FCSTD DOCUMENT  (FreeCAD 0.21R33771 (Git))
Label: Rotor_MagnetJig_Assembly
License: All rights reserved
LicenseURL: http://en.wikipedia.org/wiki/All_rights_reserved
objects: App::Link×7, Part::FeaturePython×3, Spreadsheet::Sheet×1, App::Part×1
EXTERNAL_REF file=../../../Master_of_Puppets.FCStd obj=Alternator
EXTERNAL_REF file=../../../Master_of_Puppets.FCStd obj=Fastener
EXTERNAL_REF file=../../../Master_of_Puppets.FCStd obj=Hub
EXTERNAL_REF file=../../../Master_of_Puppets.FCStd obj=Spreadsheet
EXTERNAL_REF file=../Rotor_Disk_Back.FCStd obj=Pocket001Body
EXTERNAL_REF file=../Rotor_Disk_Back_ReducedWeight.FCStd obj=Body
EXTERNAL_REF file=Rotor_MagnetJig_Inner.FCStd obj=PolarPatternBody
EXTERNAL_REF file=Rotor_MagnetJig_Outer.FCStd obj=PolarPatternBody
EXTERNAL_REF file=../Rotor_Magnets.FCStd obj=Array
EXTERNAL_REF file=../../../Fasteners/Fastener_Bolt_HubHoles.FCStd obj=Binder
EXTERNAL_REF file=../../../Fasteners/Fastener_HexNut_HubHoles.FCStd obj=Binder
EXTERNAL_REF file=../../../Fasteners/Fastener_Washer_Hub.FCStd obj=Tube
EXTERNAL_REF file=Rotor_MagnetJig_Disk.FCStd obj=PocketBody

FEATURE [Spreadsheet::Sheet] Spreadsheet
  cells = A1='Inputs; A2='RotorDiskRadius; B2(RotorDiskRadius)==Master_of_Puppets#Spreadsheet.RotorDiskRadius; A3='MagnetThickness; B3(MagnetThickness)==Master_of_Puppets#Spreadsheet.MagnetThickness; A4='RotorDiskThickness; B4(RotorDiskThickness)==Master_of_Puppets#Spreadsheet.RotorDiskThickness; A5='VaneThickness; B5(VaneThickness)==Master_of_Puppets#Spreadsheet.VaneThickness; A6='InnerDistanceBetweenMagnets; B6(InnerDistanceBetweenMagnets)==Master_of_Puppets#Spreadsheet.InnerDistanceBetweenMagnets; A7='HubPitchCircleRadius; B7(HubPitchCircleRadius)==Master_of_Puppets#Hub.HubPitchCircleRadius; A8='RotorMoldBaseThickness; B8(RotorMoldBaseThickness)==Master_of_Puppets#Alternator.RotorMoldBaseThickness; A9='MagnetJigThickness; B9(MagnetJigThickness)==Master_of_Puppets#Alternator.MagnetJigThickness; A10='NumberOfRotorMoldBolts; B10(NumberOfRotorMoldBolts)==Master_of_Puppets#Alternator.NumberOfRotorMoldBolts; A11='WasherThickness; B11(WasherThickness)==Master_of_Puppets#Fastener.WasherThickness; A12='CoilType; B12(CoilType)==Master_of_Puppets#Spreadsheet.CoilType; A13='WeightReductionRotorDiskRadiusThreshold; B13(WeightReductionRotorDiskRadiusThreshold)==Master_of_Puppets#Alternator.WeightReductionRotorDiskRadiusThreshold; A14='Calculated; A15='InnerDistanceBetweenMagnetsThreshold; B15(InnerDistanceBetweenMagnetsThreshold)=10; A16='DistanceBetweenLayers; B16(DistanceBetweenLayers)=0; A17='BoltsZ; B17(BoltsZ)==DistanceBetweenLayers * -1; A18='MagnetsZ; B18(MagnetsZ)==RotorDiskThickness + DistanceBetweenLayers * 1; A19='ShowWashers; B19(ShowWashers)==InnerDistanceBetweenMagnets < InnerDistanceBetweenMagnetsThreshold ? 0 : 1; A20='WasherZ; B20(WasherZ)==RotorDiskThickness + DistanceBetweenLayers + DistanceBetweenLayers * ShowWashers; A21='WasherZOffset; B21(WasherZOffset)==ShowWashers == 1 ? WasherThickness : 0; A22='JigZ; B22(JigZ)==RotorDiskThickness + WasherZOffset + DistanceBetweenLayers * 2 + DistanceBetweenLayers * ShowWashers; A23='NutZ; B23(NutZ)==RotorDiskThickness + WasherZOffset + MagnetJigThickness + DistanceBetweenLayers * 4; A24='Rotor_MagnetJig; B24(Rotor_MagnetJig)==InnerDistanceBetweenMagnets < InnerDistanceBetweenMagnetsThreshold ? <<Rotor_MagnetJig_Outer>>#<<Rotor_MagnetJig>>._self : <<Rotor_MagnetJig_Inner>>#<<Rotor_MagnetJig>>._self; A25='Rotor_Disk_Back; B25(Rotor_Disk_Back)==RotorDiskRadius > WeightReductionRotorDiskRadiusThreshold ? <<Rotor_Disk_Back_ReducedWeight>>#<<Rotor_Disk_Back>>._self : <<Rotor_Disk_Back>>#<<Rotor_Disk_Back>>._self; A26='ShowMagnetJigDisk; B26(ShowMagnetJigDisk)==InnerDistanceBetweenMagnets < InnerDistanceBetweenMagnetsThreshold ? 1 : 0
FEATURE [App::Link] Link004  label="Rotor_MagnetJig"
  LinkPlacement = pos=(0,0,12.5) rot=(0,0,1;0rad)
  LinkedObject = -> <external Rotor_MagnetJig_Inner.FCStd>#PolarPatternBody
  Placement = pos=(0,0,12.5) rot=(0,0,1;0rad)
  expr: .Placement.Base.z = Spreadsheet.JigZ
  expr: LinkedObject = Spreadsheet.Rotor_MagnetJig
FEATURE [App::Link] Link  label="Rotor_Disk_Back"
  LinkedObject = -> <external ../Rotor_Disk_Back_ReducedWeight.FCStd>#Body
  expr: LinkedObject = Spreadsheet.Rotor_Disk_Back
FEATURE [App::Link] Link005  label="Rotor_Magnets"
  LinkPlacement = pos=(0,0,10) rot=(0,0,1;0rad)
  LinkedObject = -> <external ../Rotor_Magnets.FCStd>#Array
  Placement = pos=(0,0,10) rot=(0,0,1;0rad)
  expr: .Placement.Base.z = Spreadsheet.MagnetsZ
FEATURE [App::Link] Link006  label="Fastener_Bolt_HubHoles"
  LinkPlacement = pos=(0,65,0) rot=(0,0,1;0rad)
  LinkedObject = -> <external ../../../Fasteners/Fastener_Bolt_HubHoles.FCStd>#Binder
  Placement = pos=(0,65,0) rot=(0,0,1;0rad)
  Scale = -1
  ScaleVector = (-1,-1,-1)
  expr: .Placement.Base.y = Spreadsheet.HubPitchCircleRadius
FEATURE [App::Link] Link007  label="Fastener_HexNut_HubHoles"
  LinkPlacement = pos=(0,65,18.5) rot=(0,0,1;0rad)
  LinkedObject = -> <external ../../../Fasteners/Fastener_HexNut_HubHoles.FCStd>#Binder
  Placement = pos=(0,65,18.5) rot=(0,0,1;0rad)
  expr: .Placement.Base.y = Spreadsheet.HubPitchCircleRadius
  expr: .Placement.Base.z = Spreadsheet.NutZ
FEATURE [Part::FeaturePython] Array  label="Bolts"  # Draft array (typed FeaturePython)
  AlwaysSyncPlacement = false
  Angle = 360
  ArrayType = 1
  Axis = (0,0,1)
  Base = -> Link006
  Center = (0,0,0)
  Count = 5
  ExpandArray = false
  Fuse = false
  IntervalAxis = (0,0,0)
  IntervalX = (50,0,0)
  IntervalY = (0,50,0)
  IntervalZ = (0,0,50)
  NumberCircles = 3
  NumberPolar = 5
  NumberX = 2
  NumberY = 2
  NumberZ = 1
  PlacementList = 5 placements: [(0,65,0),(-61.8187,20.0861,0),(-38.206,-52.5861,0),(38.206,-52.5861,0),(61.8187,20.0861,0)]
  RadialDistance = 50
  ScaleList = (5) [(1,1,1),(1,1,1),(1,1,1),(1,1,1),(1,1,1)]
  Symmetry = 1
  TangentialDistance = 25
  expr: .Placement.Base.z = Spreadsheet.BoltsZ
  expr: NumberPolar = Spreadsheet.NumberOfRotorMoldBolts
FEATURE [Part::FeaturePython] Array001  label="Nuts"  # Draft array (typed FeaturePython)
  AlwaysSyncPlacement = false
  Angle = 360
  ArrayType = 1
  Axis = (0,0,1)
  Base = -> Link007
  Center = (0,0,0)
  Count = 5
  ExpandArray = false
  Fuse = false
  IntervalAxis = (0,0,0)
  IntervalX = (50,0,0)
  IntervalY = (0,50,0)
  IntervalZ = (0,0,50)
  NumberCircles = 3
  NumberPolar = 5
  NumberX = 2
  NumberY = 2
  NumberZ = 1
  PlacementList = 5 placements: [(0,65,18.5),(-61.8187,20.0861,18.5),(-38.206,-52.5861,18.5),(38.206,-52.5861,18.5),(61.8187,20.0861,18.5)]
  RadialDistance = 50
  ScaleList = (5) [(1,1,1),(1,1,1),(1,1,1),(1,1,1),(1,1,1)]
  Symmetry = 1
  TangentialDistance = 25
  expr: NumberPolar = Spreadsheet.NumberOfRotorMoldBolts
FEATURE [App::Link] Link008  label="Fastener_Washer_Hub"
  LinkPlacement = pos=(0,65,10) rot=(0,0,1;0rad)
  LinkedObject = -> <external ../../../Fasteners/Fastener_Washer_Hub.FCStd>#Tube
  Placement = pos=(0,65,10) rot=(0,0,1;0rad)
  expr: .Placement.Base.y = Spreadsheet.HubPitchCircleRadius
  expr: .Placement.Base.z = Spreadsheet.WasherZ
FEATURE [Part::FeaturePython] Array002  label="Washers"  # Draft array (typed FeaturePython)
  AlwaysSyncPlacement = false
  Angle = 360
  ArrayType = 1
  Axis = (0,0,1)
  Base = -> Link008
  Center = (0,0,0)
  Count = 5
  ExpandArray = false
  Fuse = false
  IntervalAxis = (0,0,0)
  IntervalX = (50,0,0)
  IntervalY = (0,50,0)
  IntervalZ = (0,0,50)
  NumberCircles = 3
  NumberPolar = 5
  NumberX = 2
  NumberY = 2
  NumberZ = 1
  PlacementList = 5 placements: [(0,65,10),(-61.8187,20.0861,10),(-38.206,-52.5861,10),(38.206,-52.5861,10),(61.8187,20.0861,10)]
  RadialDistance = 50
  ScaleList = (5) [(1,1,1),(1,1,1),(1,1,1),(1,1,1),(1,1,1)]
  Symmetry = 1
  TangentialDistance = 25
  expr: NumberPolar = Spreadsheet.NumberOfRotorMoldBolts
  expr: Visibility = Spreadsheet.ShowWashers
FEATURE [App::Link] Link009  label="Rotor_MagnetJig_Disk"
  LinkPlacement = pos=(0,0,12.5) rot=(0,0,1;0rad)
  LinkedObject = -> <external Rotor_MagnetJig_Disk.FCStd>#PocketBody
  Placement = pos=(0,0,12.5) rot=(0,0,1;0rad)
  expr: .Placement.Base.z = Spreadsheet.JigZ
  expr: Visibility = Spreadsheet.ShowMagnetJigDisk
FEATURE [App::Part] Part  label="Rotor_MagnetJig_Assembly"
  Group = -> [Link006,Array,Link,Link005,Link008,Array002,Link004,Link007,Array001,Link009]
  Origin = -> Origin

RESOLVED EXTERNAL PARTS (link-assembly join: the EXTERNAL_REF files above that resolve inside this repo's crawl, each included once):
---- part ../../../Fasteners/Fastener_Bolt_HubHoles.FCStd = doc fcstd_15687eb65cfb ----
FCSTD DOCUMENT  (FreeCAD 0.20R29177 (Git))
Label: Fastener_Bolt_HubHoles
License: All rights reserved
LicenseURL: http://en.wikipedia.org/wiki/All_rights_reserved
objects: PartDesign::SubShapeBinder×1
note: 1 computed .brp shape members not serialized (recipe doc carries the construction recipe); baked Part::Feature solids carry a one-line shape summary decoded from their .brp
EXTERNAL_REF file=Fastener_Bolt_Tail_Vane.FCStd obj=Body

FEATURE [PartDesign::SubShapeBinder] Binder  label="Fastener_Bolt_HubHoles"
  BindCopyOnChange = 2
  BindMode = 0
  ClaimChildren = false
  Fuse = false
  MakeFace = true
  OffsetFill = false
  OffsetIntersection = false
  OffsetJoinType = 0
  OffsetOpenResult = false
  PartialLoad = false
  Relative = true
  Support = -> [<external Fastener_Bolt_Tail_Vane.FCStd>#Body]
  Variant = 1
  _Version = 2
---- part ../../../Fasteners/Fastener_HexNut_HubHoles.FCStd = doc fcstd_dba15245a95b ----
FCSTD DOCUMENT  (FreeCAD 0.21R33771 (Git))
Label: Fastener_HexNut_HubHoles
License: All rights reserved
LicenseURL: http://en.wikipedia.org/wiki/All_rights_reserved
objects: PartDesign::SubShapeBinder×1
note: 1 computed .brp shape members not serialized (recipe doc carries the construction recipe); baked Part::Feature solids carry a one-line shape summary decoded from their .brp
EXTERNAL_REF file=Fastener_HexNut.FCStd obj=Body

FEATURE [PartDesign::SubShapeBinder] Binder  label="Fastener_HexNut"
  BindCopyOnChange = 2
  BindMode = 0
  ClaimChildren = false
  Fuse = false
  MakeFace = true
  OffsetFill = false
  OffsetIntersection = false
  OffsetJoinType = 0
  OffsetOpenResult = false
  PartialLoad = false
  Relative = true
  Support = -> [<external Fastener_HexNut.FCStd>#Body]
  Variant = 1
  _Version = 2
---- part ../../../Master_of_Puppets.FCStd = doc fcstd_6404554055c4 (61625 chars; too large to inline — full recipe in that document) ----
---- part ../Rotor_Disk_Back.FCStd = doc fcstd_76cebaedbb85 ----
FCSTD DOCUMENT  (FreeCAD 0.20R29177 (Git))
Label: Rotor_Disk_Back
License: All rights reserved
LicenseURL: http://en.wikipedia.org/wiki/All_rights_reserved
objects: Sketcher::SketchObject×3, PartDesign::Pocket×2, PartDesign::Pad×1, PartDesign::PolarPattern×1, Spreadsheet::Sheet×1, PartDesign::Body×1
note: 11 computed .brp shape members not serialized (recipe doc carries the construction recipe); baked Part::Feature solids carry a one-line shape summary decoded from their .brp
EXTERNAL_REF file=../../Master_of_Puppets.FCStd obj=Hub
EXTERNAL_REF file=../../Master_of_Puppets.FCStd obj=Spreadsheet

FEATURE [Sketcher::SketchObject] Sketch  label="DiskSketch"
  FullyConstrained = true
  MapMode = 5
  Support = -> [XY_Plane001]
  expr: Constraints[1] = Spreadsheet.RotorDiskRadius
  sketch-geometry (1):
    g0: Circle CenterX=0 CenterY=0 CenterZ=0 NormalX=0 NormalY=0 NormalZ=1 AngleXU=0 Radius=150
  constraints (2):
    c: Coincident(g0,g-1)
    c: Radius(g0) = 150
FEATURE [PartDesign::Pad] Pad  label="Disk"
  AllowMultiFace = false
  Direction = (0,0,1)
  Length = 10
  Length2 = 100
  Profile = -> Sketch
  Type = 0
  expr: Length = Spreadsheet.RotorDiskThickness
FEATURE [Sketcher::SketchObject] Sketch001  label="HubHoleSketch"
  FullyConstrained = true
  MapMode = 5
  Placement = pos=(0,0,10) rot=(0,0,1;0rad)
  Support = -> [Pad]
  expr: Constraints[3] = Spreadsheet.HubPitchCircleRadius
  expr: Constraints[4] = Spreadsheet.HubHolesRadius
  sketch-geometry (2):
    g0: LineSegment StartX=0 StartY=50 StartZ=0 EndX=0 EndY=0 EndZ=0
    g1: Circle CenterX=0 CenterY=50 CenterZ=0 NormalX=0 NormalY=0 NormalZ=1 AngleXU=0 Radius=6
  constraints (5):
    c: Coincident(g0,g-1)
    c: Vertical(g0)
    c: Coincident(g1,g0)
    c: Distance(g0) = 50
    c: Radius(g1) = 6
FEATURE [PartDesign::Pocket] Pocket
  AllowMultiFace = false
  BaseFeature = -> Pad
  Direction = (0,0,-1)
  Length = 5
  Length2 = 100
  Profile = -> Sketch001
  Type = 1
FEATURE [PartDesign::PolarPattern] PolarPattern  label="HubHolePolarPattern"
  Angle = 360
  Axis = -> Sketch001 [N_Axis]
  BaseFeature = -> Pocket
  Occurrences = 4
  Originals = -> [Pocket]
  expr: Occurrences = Spreadsheet.NumberOfHoles
FEATURE [Sketcher::SketchObject] Sketch002  label="CentralHoleSketch"
  FullyConstrained = true
  MapMode = 5
  Placement = pos=(0,0,10) rot=(0,0,1;0rad)
  Support = -> [PolarPattern]
  expr: Constraints[1] = Spreadsheet.RotorDiskCentralHoleRadius
  sketch-geometry (1):
    g0: Circle CenterX=0 CenterY=0 CenterZ=0 NormalX=0 NormalY=0 NormalZ=1 AngleXU=0 Radius=32.5
  constraints (2):
    c: Coincident(g0,g-1)
    c: Radius(g0) = 32.5
FEATURE [PartDesign::Pocket] Pocket001  label="CentralHole"
  AllowMultiFace = false
  BaseFeature = -> PolarPattern
  Direction = (0,0,-1)
  Length = 5
  Length2 = 100
  Profile = -> Sketch002
  Type = 1
FEATURE [Spreadsheet::Sheet] Spreadsheet
  cells = A1=Inputs; A2=RotorDiskRadius; B2(RotorDiskRadius)==Master_of_Puppets#Spreadsheet.RotorDiskRadius; A3=RotorDiskCentralHoleDiameter; B3(RotorDiskCentralHoleDiameter)==Master_of_Puppets#Spreadsheet.RotorDiskCentralHoleDiameter; A4=HubPitchCircleRadius; B4(HubPitchCircleRadius)==Master_of_Puppets#Hub.HubPitchCircleRadius; A5=RotorDiskThickness; B5(RotorDiskThickness)==Master_of_Puppets#Spreadsheet.RotorDiskThickness; A6=HubHolesRadius; B6(HubHolesRadius)==Master_of_Puppets#Hub.HubHolesRadius; A7=NumberOfHoles; B7(NumberOfHoles)==Master_of_Puppets#Hub.NumberOfHoles; A8=Calculated; A9=RotorDiskCentralHoleRadius; B9(RotorDiskCentralHoleRadius)==RotorDiskCentralHoleDiameter / 2
FEATURE [PartDesign::Body] Pocket001Body  label="Rotor_Disk_Back"
  Group = -> [Sketch,Pad,Sketch001,Pocket,PolarPattern,Sketch002,Pocket001]
  Openafpm_Flat = true
  Origin = -> Origin001
  Placement = pos=(4e-15,0,0) rot=(0,0,1;0rad)
  Tip = -> Pocket001
---- part ../Rotor_Disk_Back_ReducedWeight.FCStd = doc fcstd_80efc63f53a1 ----
FCSTD DOCUMENT  (FreeCAD 0.21R33771 (Git))
Label: Rotor_Disk_Back_ReducedWeight
License: All rights reserved
LicenseURL: http://en.wikipedia.org/wiki/All_rights_reserved
objects: Sketcher::SketchObject×3, PartDesign::Pocket×2, PartDesign::PolarPattern×2, PartDesign::Pad×1, Spreadsheet::Sheet×1, PartDesign::Mirrored×1, PartDesign::MultiTransform×1, PartDesign::Body×1
note: 14 computed .brp shape members not serialized (recipe doc carries the construction recipe); baked Part::Feature solids carry a one-line shape summary decoded from their .brp
EXTERNAL_REF file=../../Master_of_Puppets.FCStd obj=Alternator
EXTERNAL_REF file=../../Master_of_Puppets.FCStd obj=Hub
EXTERNAL_REF file=../../Master_of_Puppets.FCStd obj=Spreadsheet

FEATURE [Sketcher::SketchObject] Sketch  label="DiskSketch"
  FullyConstrained = true
  MapMode = 5
  Support = -> [XY_Plane]
  expr: Constraints[1] = Spreadsheet.RotorDiskRadius
  expr: Constraints[2] = Spreadsheet.RotorDiskCentralHoleRadius
  sketch-geometry (2):
    g0: Circle CenterX=0 CenterY=0 CenterZ=0 NormalX=0 NormalY=0 NormalZ=1 AngleXU=0 Radius=250
    g1: Circle CenterX=0 CenterY=0 CenterZ=0 NormalX=0 NormalY=0 NormalZ=1 AngleXU=0 Radius=47.5
  constraints (4):
    c: Coincident(g0,g-1)
    c: Radius(g0) = 250
    c: Radius(g1) = 47.5
    c: Coincident(g1,g0)
FEATURE [PartDesign::Pad] Pad  label="Disk"
  AllowMultiFace = false
  Direction = (0,0,1)
  Length = 10
  Length2 = 100
  Profile = -> Sketch
  Type = 0
  expr: Length = Spreadsheet.RotorDiskThickness
FEATURE [Sketcher::SketchObject] Sketch001  label="PocketSketch"
  FullyConstrained = true
  MapMode = 5
  Placement = pos=(0,0,10) rot=(0,0,1;0rad)
  Support = -> [Pad]
  expr: Constraints[12] = Spreadsheet.WidthOuterPocket / 2
  expr: Constraints[13] = Spreadsheet.WidthInnerPocket / 2
  expr: Constraints[2] = Spreadsheet.PocketOuterRadius
  expr: Constraints[3] = Spreadsheet.PocketInnerRadius
  sketch-geometry (6):
    g0: Circle CenterX=0 CenterY=0 CenterZ=0 NormalX=0 NormalY=0 NormalZ=1 AngleXU=0 Radius=86
    g1: Circle CenterX=0 CenterY=0 CenterZ=0 NormalX=0 NormalY=0 NormalZ=1 AngleXU=0 Radius=167
    g2: LineSegment StartX=22.5147 StartY=83.0005 StartZ=0 EndX=43.7205 EndY=161.175 EndZ=0
    g3: LineSegment StartX=5.3e-15 StartY=86 StartZ=0 EndX=5.3e-15 EndY=167 EndZ=0
    g4: ArcOfCircle CenterX=0 CenterY=5.0665e-12 CenterZ=0 NormalX=0 NormalY=0 NormalZ=1 AngleXU=0 Radius=86 StartAngle=1.30591 EndAngle=1.5708
    g5: ArcOfCircle CenterX=0 CenterY=5.0665e-12 CenterZ=0 NormalX=0 NormalY=0 NormalZ=1 AngleXU=0 Radius=167 StartAngle=1.30591 EndAngle=1.5708
  constraints (17):
    c: Coincident(g0,g-1)
    c: Coincident(g1,g-1)
    c: Radius(g1) = 167
    c: Radius(g0) = 86
    c: PointOnObject(g3,g0)
    c: PointOnObject(g3,g1)
    c: Vertical(g3)
    c: Coincident(g4,g2)
    c: Coincident(g4,g3)
    c: PointOnObject(g5,g-2)
    c: Coincident(g5,g2)
    c: Coincident(g5,g3)
    c: DistanceX(g-1,g2) = 43.7205
    c: DistanceX(g-1,g2) = 22.5147
    c: PointOnObject(g2,g1)
    c: DistanceX(g-1,g3) = 0
    c: Coincident(g4,g5)
FEATURE [PartDesign::Pocket] Pocket  label="PocketPocket"
  AllowMultiFace = false
  BaseFeature = -> Pad
  Direction = (0,0,-1)
  Length = 5
  Length2 = 100
  Profile = -> Sketch001
  Type = 1
FEATURE [Spreadsheet::Sheet] Spreadsheet
  cells = A1='Inputs; A2='Spreadsheet; A3='HubHolesRadius; B3(HubHolesRadius)==Master_of_Puppets#Hub.HubHolesRadius; A4='RotorDiskRadius; B4(RotorDiskRadius)==Master_of_Puppets#Spreadsheet.RotorDiskRadius; A5='RotorDiskCentralHoleDiameter; B5(RotorDiskCentralHoleDiameter)==Master_of_Puppets#Spreadsheet.RotorDiskCentralHoleDiameter; A6='HubPitchCircleRadius; B6(HubPitchCircleRadius)==Master_of_Puppets#Hub.HubPitchCircleRadius; A7='RotorDiskThickness; B7(RotorDiskThickness)==Master_of_Puppets#Spreadsheet.RotorDiskThickness; A8='Alternator; A9='NumberOfPockets; B9(NumberOfPockets)==Master_of_Puppets#Alternator.NumberOfPockets; A10='PocketInnerRadius; B10(PocketInnerRadius)==Master_of_Puppets#Alternator.PocketInnerRadius; A11='PocketOuterRadius; B11(PocketOuterRadius)==Master_of_Puppets#Alternator.PocketOuterRadius; A12='WidthInnerPocket; B12(WidthInnerPocket)==Master_of_Puppets#Alternator.WidthInnerPocket; A13='WidthOuterPocket; B13(WidthOuterPocket)==Master_of_Puppets#Alternator.WidthOuterPocket; A14='Hub; A15='NumberOfHoles; B15(NumberOfHoles)==Master_of_Puppets#Hub.NumberOfHoles; A16='Calculated; A17='RotorDiskCentralHoleRadius; B17(RotorDiskCentralHoleRadius)==RotorDiskCentralHoleDiameter / 2
FEATURE [Sketcher::SketchObject] Sketch002  label="HoleSketch"
  FullyConstrained = true
  MapMode = 5
  Placement = pos=(0,0,10) rot=(0,0,1;0rad)
  Support = -> [Pad]
  expr: Constraints[1] = Spreadsheet.HubPitchCircleRadius
  expr: Constraints[4] = Spreadsheet.HubHolesRadius
  sketch-geometry (2):
    g0: Circle CenterX=0 CenterY=0 CenterZ=0 NormalX=0 NormalY=0 NormalZ=1 AngleXU=0 Radius=65
    g1: Circle CenterX=0 CenterY=65 CenterZ=0 NormalX=0 NormalY=0 NormalZ=1 AngleXU=0 Radius=7
  constraints (5):
    c: Coincident(g0,g-1)
    c: Radius(g0) = 65
    c: PointOnObject(g1,g0)
    c: PointOnObject(g1,g-2)
    c: Radius(g1) = 7
FEATURE [PartDesign::Mirrored] Mirrored
  MirrorPlane = -> Sketch001 [V_Axis]
FEATURE [PartDesign::PolarPattern] PolarPattern
  Angle = 360
  Axis = -> Sketch001 [N_Axis]
  Occurrences = 6
  expr: Occurrences = Spreadsheet.NumberOfPockets
FEATURE [PartDesign::MultiTransform] MultiTransform  label="PocketMultiTransform"
  BaseFeature = -> Pocket
  Originals = -> [Pocket]
  Transformations = -> [Mirrored,PolarPattern]
FEATURE [PartDesign::Pocket] Pocket001  label="HolePocket"
  BaseFeature = -> MultiTransform
  Direction = (0,0,-1)
  Length = 5
  Length2 = 5
  Profile = -> Sketch002
  ReferenceAxis = -> Sketch002 [N_Axis]
  Type = 1
FEATURE [PartDesign::PolarPattern] PolarPattern001  label="HolePolarPattern"
  Angle = 360
  Axis = -> Sketch002 [N_Axis]
  BaseFeature = -> Pocket001
  Occurrences = 5
  Originals = -> [Pocket001]
  expr: Occurrences = Spreadsheet.NumberOfHoles
FEATURE [PartDesign::Body] Body  label="Rotor_Disk_Back"
  Group = -> [Sketch,Pad,Sketch001,Pocket,MultiTransform,Sketch002,Mirrored,PolarPattern,Pocket001,PolarPattern001]
  Openafpm_Flat = true
  Origin = -> Origin
  Tip = -> PolarPattern001
---- part ../Rotor_Magnets.FCStd = doc fcstd_047787b4cc6b ----
FCSTD DOCUMENT  (FreeCAD 0.20R29177 (Git))
Label: Rotor_Magnets
License: All rights reserved
LicenseURL: http://en.wikipedia.org/wiki/All_rights_reserved
objects: App::Link×1, Spreadsheet::Sheet×1, Part::FeaturePython×1
EXTERNAL_REF file=Rotor_Magnet.FCStd obj=Box
EXTERNAL_REF file=../../Master_of_Puppets.FCStd obj=Alternator
EXTERNAL_REF file=../../Master_of_Puppets.FCStd obj=Spreadsheet

FEATURE [App::Link] Link  label="Magnet"
  LinkPlacement = pos=(-25,97.902,0) rot=(0,0,1;0rad)
  LinkedObject = -> <external Rotor_Magnet.FCStd>#Box
  Placement = pos=(-25,97.902,0) rot=(0,0,1;0rad)
  expr: .Placement.Base.x = Spreadsheet.MagnetX
  expr: .Placement.Base.y = Spreadsheet.MagnetY
FEATURE [Spreadsheet::Sheet] Spreadsheet
  cells = A1=Inputs; A2=MagnetWidth; B2(MagnetWidth)==Master_of_Puppets#Spreadsheet.MagnetWidth; A3=MagnetLength; B3(MagnetLength)==Master_of_Puppets#Spreadsheet.MagnetLength; A4=RotorDiskRadius; B4(RotorDiskRadius)==Master_of_Puppets#Spreadsheet.RotorDiskRadius; A5=NumberMagnet; B5(NumberMagnet)==Master_of_Puppets#Spreadsheet.NumberMagnet; A6=DistanceOfMagnetFromCenter; B6(DistanceOfMagnetFromCenter)==Master_of_Puppets#Alternator.DistanceOfMagnetFromCenter; A7=Magnet; A8=MagnetX; B8(MagnetX)==-MagnetWidth / 2; A9=MagnetY; B9(MagnetY)==DistanceOfMagnetFromCenter
FEATURE [Part::FeaturePython] Array  label="Rotor_Magnets"  # Draft array (typed FeaturePython)
  AlwaysSyncPlacement = false
  Angle = 360
  ArrayType = 1
  Axis = (0,0,1)
  Base = -> Link
  Center = (0,0,0)
  Count = 12
  ExpandArray = false
  Fuse = false
  IntervalAxis = (0,0,0)
  IntervalX = (50,0,0)
  IntervalY = (0,50,0)
  IntervalZ = (0,0,50)
  NumberCircles = 3
  NumberPolar = 12
  NumberX = 2
  NumberY = 2
  NumberZ = 1
  Placement = pos=(3.6e-15,0,0) rot=(0,0,1;0rad)
  PlacementList = 12 placements: [(-25,97.902,0),(-70.6016,72.2856,0),(-97.2856,27.3004,0),(-97.902,-25,0),(-72.2856,-70.6016,0),(-27.3004,-97.2856,0),(25,-97.902,0),(70.6016,-72.2856,0),(97.2856,-27.3004,0),(97.902,25,0),(72.2856,70.6016,0),(27.3004,97.2856,0)]
  RadialDistance = 50
  ScaleList = (12) [(1,1,1),(1,1,1),(1,1,1),(1,1,1),(1,1,1),(1,1,1),(1,1,1),(1,1,1),(1,1,1),(1,1,1),(1,1,1),(1,1,1)]
  Symmetry = 1
  TangentialDistance = 25
  expr: NumberPolar = Spreadsheet.NumberMagnet
---- part Rotor_MagnetJig_Disk.FCStd = doc fcstd_5108bd749691 ----
FCSTD DOCUMENT  (FreeCAD 0.20R29177 (Git))
Label: Rotor_MagnetJig_Disk
Comment: Similar to Rotor_Mold_Island with varying radius and thickness.
License: All rights reserved
LicenseURL: http://en.wikipedia.org/wiki/All_rights_reserved
objects: Sketcher::SketchObject×2, PartDesign::Pad×1, PartDesign::Pocket×1, Spreadsheet::Sheet×1, PartDesign::PolarPattern×1, PartDesign::Body×1
note: 8 computed .brp shape members not serialized (recipe doc carries the construction recipe); baked Part::Feature solids carry a one-line shape summary decoded from their .brp
EXTERNAL_REF file=../../../Master_of_Puppets.FCStd obj=Alternator
EXTERNAL_REF file=../../../Master_of_Puppets.FCStd obj=Hub
EXTERNAL_REF file=../../../Master_of_Puppets.FCStd obj=Spreadsheet

FEATURE [Sketcher::SketchObject] Sketch
  FullyConstrained = true
  MapMode = 5
  Support = -> [XY_Plane001]
  expr: Constraints[1] = Spreadsheet.DistanceOfMagnetFromCenter
  sketch-geometry (1):
    g0: Circle CenterX=0 CenterY=0 CenterZ=0 NormalX=0 NormalY=0 NormalZ=1 AngleXU=0 Radius=103.248
  constraints (2):
    c: Coincident(g0,g-1)
    c: Radius(g0) = 103.248
FEATURE [PartDesign::Pad] Pad
  AllowMultiFace = false
  Direction = (0,0,1)
  Length = 6
  Length2 = 100
  Profile = -> Sketch
  Type = 0
  expr: Length = Spreadsheet.MagnetJigThickness
FEATURE [Sketcher::SketchObject] Sketch001
  FullyConstrained = true
  MapMode = 5
  Placement = pos=(0,0,6) rot=(0,0,1;0rad)
  Support = -> [Pad]
  expr: Constraints[3] = Spreadsheet.HubPitchCircleRadius
  expr: Constraints[4] = Spreadsheet.HubHolesRadius
  sketch-geometry (2):
    g0: LineSegment StartX=0 StartY=50 StartZ=0 EndX=0 EndY=0 EndZ=0
    g1: Circle CenterX=0 CenterY=50 CenterZ=0 NormalX=0 NormalY=0 NormalZ=1 AngleXU=0 Radius=6
  constraints (5):
    c: Coincident(g0,g-1)
    c: Vertical(g0)
    c: Coincident(g1,g0)
    c: Distance(g0) = 50
    c: Radius(g1) = 6
FEATURE [PartDesign::Pocket] Pocket
  AllowMultiFace = false
  BaseFeature = -> Pad
  Direction = (0,0,-1)
  Length = 5
  Length2 = 100
  Profile = -> Sketch001
  Type = 1
FEATURE [Spreadsheet::Sheet] Spreadsheet
  cells = A1=Inputs; A2=HubHolesRadius; B2(HubHolesRadius)==Master_of_Puppets#Hub.HubHolesRadius; A3=HubPitchCircleRadius; B3(HubPitchCircleRadius)==Master_of_Puppets#Hub.HubPitchCircleRadius; A4=MagnetThickness; B4(MagnetThickness)==Master_of_Puppets#Spreadsheet.MagnetThickness; A5=NumberOfRotorMoldBolts; B5(NumberOfRotorMoldBolts)==Master_of_Puppets#Alternator.NumberOfRotorMoldBolts; A6=MagnetJigThickness; B6(MagnetJigThickness)==Master_of_Puppets#Alternator.MagnetJigThickness; A7=DistanceOfMagnetFromCenter; B7(DistanceOfMagnetFromCenter)==Master_of_Puppets#Alternator.DistanceOfMagnetFromCenter
FEATURE [PartDesign::PolarPattern] PolarPattern
  Angle = 360
  Axis = -> Sketch001 [N_Axis]
  BaseFeature = -> Pocket
  Occurrences = 2
  Originals = -> [Pocket]
  expr: Occurrences = Spreadsheet.NumberOfRotorMoldBolts
FEATURE [PartDesign::Body] PocketBody  label="Rotor_MagnetJig_Disk"
  Group = -> [Sketch,Pad,Sketch001,Pocket,PolarPattern]
  Openafpm_Flat = true
  Origin = -> Origin001
  Tip = -> PolarPattern
---- part Rotor_MagnetJig_Inner.FCStd = doc fcstd_12b98af02b98 ----
FCSTD DOCUMENT  (FreeCAD 0.20R29177 (Git))
Label: Rotor_MagnetJig_Inner
License: All rights reserved
LicenseURL: http://en.wikipedia.org/wiki/All_rights_reserved
objects: Sketcher::SketchObject×3, PartDesign::Pocket×2, PartDesign::PolarPattern×2, PartDesign::Pad×1, Spreadsheet::Sheet×1, PartDesign::Body×1
note: 12 computed .brp shape members not serialized (recipe doc carries the construction recipe); baked Part::Feature solids carry a one-line shape summary decoded from their .brp
EXTERNAL_REF file=../../../Master_of_Puppets.FCStd obj=Alternator
EXTERNAL_REF file=../../../Master_of_Puppets.FCStd obj=Hub
EXTERNAL_REF file=../../../Master_of_Puppets.FCStd obj=Spreadsheet

FEATURE [Sketcher::SketchObject] Sketch  label="RotorDiskSketch"
  FullyConstrained = true
  MapMode = 5
  Support = -> [XY_Plane001]
  expr: Constraints[1] = Spreadsheet.RotorDiskRadius
  sketch-geometry (1):
    g0: Circle CenterX=0 CenterY=0 CenterZ=0 NormalX=0 NormalY=0 NormalZ=1 AngleXU=0 Radius=150
  constraints (2):
    c: Coincident(g0,g-1)
    c: Radius(g0) = 150
FEATURE [PartDesign::Pad] Pad  label="RotorDiskPad"
  AllowMultiFace = false
  Direction = (0,0,1)
  Length = 6
  Length2 = 100
  Profile = -> Sketch
  Type = 0
  expr: Length = Spreadsheet.MagnetJigThickness
FEATURE [Sketcher::SketchObject] Sketch001  label="HolesSketch"
  FullyConstrained = true
  MapMode = 5
  Placement = pos=(0,0,6) rot=(0,0,1;0rad)
  Support = -> [Pad]
  expr: Constraints[1] = Spreadsheet.HubHolesRadius
  expr: Constraints[2] = Spreadsheet.HubPitchCircleRadius
  sketch-geometry (1):
    g0: Circle CenterX=0 CenterY=50 CenterZ=0 NormalX=0 NormalY=0 NormalZ=1 AngleXU=0 Radius=6
  constraints (3):
    c: PointOnObject(g0,g-2)
    c: Radius(g0) = 6
    c: DistanceY(g-1,g0) = 50
FEATURE [PartDesign::Pocket] Pocket  label="HolesPocket"
  AllowMultiFace = false
  BaseFeature = -> Pad
  Direction = (0,0,-1)
  Length = 5
  Length2 = 100
  Profile = -> Sketch001
  Type = 1
FEATURE [Sketcher::SketchObject] Sketch002  label="MagnetSketch"
  FullyConstrained = true
  MapMode = 5
  Placement = pos=(0,0,6) rot=(0,0,1;0rad)
  Support = -> [Pocket]
  expr: Constraints[4] = Spreadsheet.MagnetWidth
  expr: Constraints[5] = Spreadsheet.MagnetLength
  expr: Constraints[7] = Spreadsheet.RotorDiskRadius
  sketch-geometry (5):
    g0: LineSegment StartX=15 StartY=150 StartZ=0 EndX=15 EndY=104 EndZ=0
    g1: LineSegment StartX=15 StartY=104 StartZ=0 EndX=-15 EndY=104 EndZ=0
    g2: LineSegment StartX=-15 StartY=104 StartZ=0 EndX=-15 EndY=150 EndZ=0
    g3: Circle CenterX=0 CenterY=0 CenterZ=0 NormalX=0 NormalY=0 NormalZ=1 AngleXU=0 Radius=150
    g4: LineSegment StartX=-15 StartY=150 StartZ=0 EndX=15 EndY=150 EndZ=0
  constraints (13):
    c: Coincident(g0,g1)
    c: Coincident(g1,g2)
    c: Vertical(g0)
    c: Vertical(g2)
    c: DistanceX(g2,g0) = 30
    c: DistanceY(g2,g2) = 46
    c: Coincident(g3,g-1)
    c: Radius(g3) = 150
    c: Coincident(g4,g2)
    c: Coincident(g4,g0)
    c: Horizontal(g4)
    c: Tangent(g4,g3)
    c: Symmetric(g0,g1,g-2)
FEATURE [PartDesign::Pocket] Pocket001  label="MagnetPocket"
  AllowMultiFace = false
  BaseFeature = -> Pocket
  Direction = (0,0,-1)
  Length = 5
  Length2 = 100
  Profile = -> Sketch002
  Type = 1
FEATURE [PartDesign::PolarPattern] PolarPattern  label="MagnetPolarPattern"
  Angle = 360
  Axis = -> Sketch002 [N_Axis]
  BaseFeature = -> Pocket001
  Occurrences = 12
  Originals = -> [Pocket001]
  expr: Occurrences = Spreadsheet.NumberMagnet
FEATURE [Spreadsheet::Sheet] Spreadsheet
  cells = A1=Inputs; A2=RotorDiskRadius; B2(RotorDiskRadius)==Master_of_Puppets#Spreadsheet.RotorDiskRadius; A3=HubHolesRadius; B3(HubHolesRadius)==Master_of_Puppets#Hub.HubHolesRadius; A4=HubPitchCircleRadius; B4(HubPitchCircleRadius)==Master_of_Puppets#Hub.HubPitchCircleRadius; A5=MagnetWidth; B5(MagnetWidth)==Master_of_Puppets#Spreadsheet.MagnetWidth; A6=MagnetLength; B6(MagnetLength)==Master_of_Puppets#Spreadsheet.MagnetLength; A7=NumberMagnet; B7(NumberMagnet)==Master_of_Puppets#Spreadsheet.NumberMagnet; A8=NumberOfRotorMoldBolts; B8(NumberOfRotorMoldBolts)==Master_of_Puppets#Alternator.NumberOfRotorMoldBolts; A9=MagnetJigThickness; B9(MagnetJigThickness)==Master_of_Puppets#Alternator.MagnetJigThickness
FEATURE [PartDesign::PolarPattern] PolarPattern001  label="HolesPolarPattern"
  Angle = 360
  Axis = -> Sketch001 [N_Axis]
  BaseFeature = -> PolarPattern
  Occurrences = 2
  Originals = -> [Pocket]
  expr: Occurrences = Spreadsheet.NumberOfRotorMoldBolts
FEATURE [PartDesign::Body] PolarPatternBody  label="Rotor_MagnetJig"
  Group = -> [Sketch,Pad,Sketch001,Pocket,Sketch002,Pocket001,PolarPattern,PolarPattern001]
  Openafpm_Flat = true
  Origin = -> Origin001
  Tip = -> PolarPattern001
---- part Rotor_MagnetJig_Outer.FCStd = doc fcstd_f523b8629cb4 ----
FCSTD DOCUMENT  (FreeCAD 0.20R29177 (Git))
Label: Rotor_MagnetJig_Outer
License: All rights reserved
LicenseURL: http://en.wikipedia.org/wiki/All_rights_reserved
objects: Sketcher::SketchObject×3, PartDesign::Pocket×2, Spreadsheet::Sheet×1, PartDesign::Pad×1, PartDesign::PolarPattern×1, PartDesign::Body×1
note: 11 computed .brp shape members not serialized (recipe doc carries the construction recipe); baked Part::Feature solids carry a one-line shape summary decoded from their .brp
EXTERNAL_REF file=../../../Master_of_Puppets.FCStd obj=Alternator
EXTERNAL_REF file=../../../Master_of_Puppets.FCStd obj=Spreadsheet

FEATURE [Sketcher::SketchObject] Sketch002  label="MagnetSketch"
  FullyConstrained = true
  MapMode = 5
  Placement = pos=(0,0,6) rot=(0,0,1;0rad)
  expr: .Placement.Base.z = Spreadsheet.MagnetJigThickness
  expr: Constraints[13] = Spreadsheet.DistanceOfMagnetFromCenter
  expr: Constraints[4] = Spreadsheet.MagnetWidth
  expr: Constraints[5] = Spreadsheet.MagnetLength
  sketch-geometry (5):
    g0: LineSegment StartX=25 StartY=147.902 StartZ=0 EndX=25 EndY=97.902 EndZ=0
    g1: LineSegment StartX=25 StartY=97.902 StartZ=0 EndX=-25 EndY=97.902 EndZ=0
    g2: LineSegment StartX=-25 StartY=97.902 StartZ=0 EndX=-25 EndY=147.902 EndZ=0
    g3: LineSegment StartX=-25 StartY=147.902 StartZ=0 EndX=25 EndY=147.902 EndZ=0
    g4: LineSegment StartX=0 StartY=0 StartZ=0 EndX=0 EndY=97.902 EndZ=0
  constraints (14):
    c: Coincident(g0,g1)
    c: Coincident(g1,g2)
    c: Vertical(g0)
    c: Vertical(g2)
    c: DistanceX(g2,g0) = 50
    c: DistanceY(g2,g2) = 50
    c: Coincident(g3,g2)
    c: Coincident(g3,g0)
    c: Horizontal(g3)
    c: Symmetric(g0,g1,g-2)
    c: Coincident(g4,g-1)
    c: PointOnObject(g4,g1)
    c: Vertical(g4)
    c: DistanceY(g4,g4) = 97.902
FEATURE [Spreadsheet::Sheet] Spreadsheet
  cells = A1=Inputs; A2=RotorDiskRadius; B2(RotorDiskRadius)==Master_of_Puppets#Spreadsheet.RotorDiskRadius; A3=MagnetWidth; B3(MagnetWidth)==Master_of_Puppets#Spreadsheet.MagnetWidth; A4=MagnetLength; B4(MagnetLength)==Master_of_Puppets#Spreadsheet.MagnetLength; A5=NumberMagnet; B5(NumberMagnet)==Master_of_Puppets#Spreadsheet.NumberMagnet; A6=RotorMoldSideLength; B6(RotorMoldSideLength)==Master_of_Puppets#Alternator.RotorMoldSideLength; A7=MagnetJigThickness; B7(MagnetJigThickness)==Master_of_Puppets#Alternator.MagnetJigThickness; A8=DistanceOfMagnetFromCenter; B8(DistanceOfMagnetFromCenter)==Master_of_Puppets#Alternator.DistanceOfMagnetFromCenter; A9=Calculated; A10=Inradius; B10(Inradius)==DistanceOfMagnetFromCenter; A11=SideLength; B11(SideLength)==2 * Inradius * tan(180 / NumberMagnet); C11=https://keisan.casio.com/exec/system/1223432660; A12=InnerHoleRadius; B12(InnerHoleRadius)==SideLength / (2 * sin(180 / NumberMagnet)); C12=https://www-formula.com/geometry/radius-circumcircle/radius-circumcircle-regular-polygon
FEATURE [Sketcher::SketchObject] Sketch  label="SquareSketch"
  FullyConstrained = true
  MapMode = 5
  Support = -> [XY_Plane001]
  expr: Constraints[6] = Spreadsheet.RotorMoldSideLength
  sketch-geometry (4):
    g0: LineSegment StartX=-199.995 StartY=-199.995 StartZ=0 EndX=199.995 EndY=-199.995 EndZ=0
    g1: LineSegment StartX=199.995 StartY=-199.995 StartZ=0 EndX=199.995 EndY=199.995 EndZ=0
    g2: LineSegment StartX=199.995 StartY=199.995 StartZ=0 EndX=-199.995 EndY=199.995 EndZ=0
    g3: LineSegment StartX=-199.995 StartY=199.995 StartZ=0 EndX=-199.995 EndY=-199.995 EndZ=0
  constraints (10):
    c: Coincident(g0,g1)
    c: Coincident(g1,g2)
    c: Coincident(g2,g3)
    c: Coincident(g3,g0)
    c: Horizontal(g2)
    c: Vertical(g3)
    c: DistanceX(g2,g2) = 399.99
    c: Equal(g3,g0)
    c: Symmetric(g1,g0,g-1)
    c: Symmetric(g0,g0,g-2)
FEATURE [PartDesign::Pad] Pad  label="SquarePad"
  AllowMultiFace = false
  Direction = (0,0,1)
  Length = 6
  Length2 = 100
  Profile = -> Sketch
  Type = 0
  expr: Length = Spreadsheet.MagnetJigThickness
FEATURE [PartDesign::Pocket] Pocket001  label="MagnetPocket"
  AllowMultiFace = false
  BaseFeature = -> Pad
  Direction = (0,0,-1)
  Length = 5
  Length2 = 100
  Profile = -> Sketch002
  Type = 1
FEATURE [PartDesign::PolarPattern] PolarPattern  label="MagnetPolarPattern"
  Angle = 360
  Axis = -> Sketch002 [N_Axis]
  BaseFeature = -> Pocket001
  Occurrences = 12
  Originals = -> [Pocket001]
  expr: Occurrences = Spreadsheet.NumberMagnet
FEATURE [Sketcher::SketchObject] Sketch003  label="InnerHoleSketch"
  FullyConstrained = true
  MapMode = 5
  Placement = pos=(0,0,0) rot=(0,1,0;3.14159rad)
  Support = -> [XY_Plane001]
  expr: Constraints[1] = Spreadsheet.InnerHoleRadius
  sketch-geometry (1):
    g0: Circle CenterX=0 CenterY=0 CenterZ=0 NormalX=0 NormalY=0 NormalZ=1 AngleXU=0 Radius=101.356
  constraints (2):
    c: Coincident(g0,g-1)
    c: Radius(g0) = 101.356
FEATURE [PartDesign::Pocket] Pocket  label="InnerHolePocket"
  BaseFeature = -> PolarPattern
  Direction = (0,0,1)
  Length = 4
  Length2 = 100
  Profile = -> Sketch003
  Type = 1
FEATURE [PartDesign::Body] PolarPatternBody  label="Rotor_MagnetJig"
  Group = -> [Sketch,Pad,Sketch002,Pocket001,PolarPattern,Sketch003,Pocket]
  Openafpm_Flat = true
  Origin = -> Origin001
  Tip = -> Pocket
